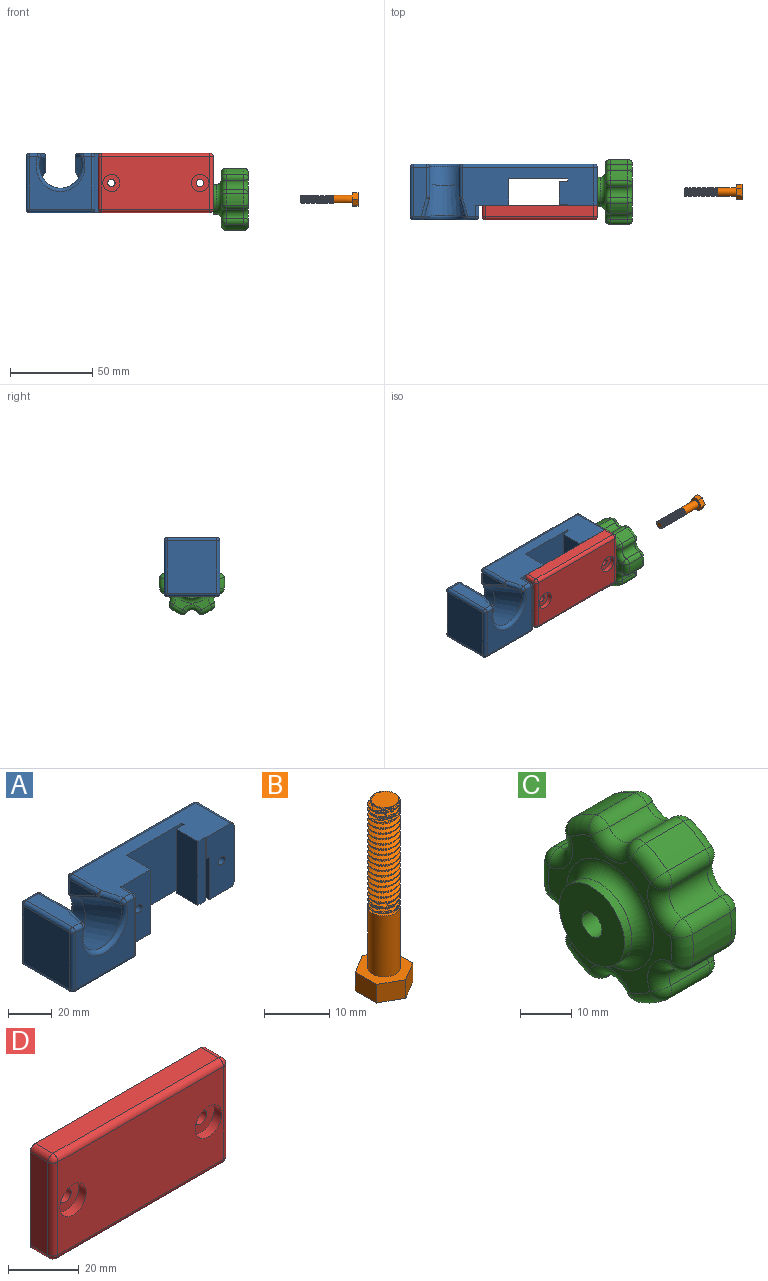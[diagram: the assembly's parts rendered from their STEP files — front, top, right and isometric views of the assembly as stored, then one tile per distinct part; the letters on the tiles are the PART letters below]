
ASSEMBLY  parts=4 mates=3
PART A: 102 faces, bbox 114x44.5x39.6 mm
  f0: cylinder r=2.6mm len=5.5mm, axis (1,0,0), area 89.8mm2, adj f7,f54
  f1: plane 32x23mm, normal (1,0,0), area 640.2mm2, adj f2,f13,f24,f47,f48,f49,f50,f56
  f2: cylinder r=5.5mm len=2.97mm, axis (1,0,0), area 0.3mm2, adj f1,f3,f47
  f3: plane 2.97x0.2mm, normal (1,0,0), area 0.4mm2, adj f2,f47
  f4: cylinder r=2.25mm len=20mm, axis (0,1,0), area 282.7mm2, adj f18,f46
  f5: cylinder r=2.25mm len=20mm, axis (0,1,0), area 282.7mm2, adj f13,f39
  f6: plane 12x1.5mm, normal (-1,0,0), area 18mm2, adj f8,f20,f26,f32
  f7: plane 24x16mm, normal (-1,0,0), area 362.8mm2, adj f0,f8,f13,f21,f26
  f8: plane 38x36mm, normal (0,-1,0), area 1344mm2, adj f6,f7,f19,f20,f21,f26
  f9: cylinder r=2.6mm len=5.4mm, axis (1,0,0), area 88.2mm2, adj f25,f52
  f10: plane 18.62x8.47mm, normal (1,0,0), area 82.6mm2, adj f83,f90,f93,f94
  f11: plane 18.62x8.47mm, normal (-1,0,0), area 82.6mm2, adj f64,f65,f70,f71
  f12: plane 30x8mm, normal (0,0,1), area 220.9mm2, adj f82,f88,f93,f96,f99
  f13: plane 36x18mm, normal (0,-1,0), area 582.4mm2, adj f1,f5,f7,f20,f21,f26,f27,f56
  f14: plane 110x32mm, normal (0,1,0), area 2724.2mm2, adj f33,f34,f35,f36,f37,f38,f40,f41
  f15: plane 32x30mm, normal (-1,0,0), area 960mm2, adj f75,f76,f87,f88
  f16: plane 38x32mm, normal (0,-1,0), area 689.8mm2, adj f73,f74,f86,f87,f95,f96
  f17: plane 32x7mm, normal (1,0,0), area 224mm2, adj f18,f62,f72,f73
  f18: plane 36x20mm, normal (0,-1,0), area 633.8mm2, adj f4,f17,f19,f20,f21,f62,f72
  f19: plane 36x16mm, normal (1,0,0), area 576mm2, adj f8,f18,f20,f21
  f20: plane 80x30mm, normal (0,0,1), area 1370.9mm2, adj f6,f8,f13,f18,f19,f27,f28,f31
  f21: plane 110x30mm, normal (0,0,-1), area 2138mm2, adj f7,f8,f13,f18,f19,f52,f53,f54
  f22: cone r=11.38mm half-angle=3.6deg, axis (0,-0.94,0.34), area 1167.2mm2, adj f23,f70,f85,f94,f95,f99
  f23: cylinder r=11.38mm len=22.76mm, axis (0,0.94,-0.34), area 475.7mm2, adj f22,f65,f70,f77,f90,f94
  f24: cylinder r=5.5mm len=11mm, axis (1,0,0), area 3.1mm2, adj f1,f25,f48
  f25: plane 11x10.7mm, normal (1,0,0), area 73.1mm2, adj f9,f24,f48
  f26: plane 16x2mm, normal (0,0,-1), area 32mm2, adj f6,f7,f8,f13,f27,f30
  f27: plane 12x0.5mm, normal (-1,0,0), area 6mm2, adj f13,f20,f26,f28
  f28: plane 36x5mm, normal (0,-1,0), area 180mm2, adj f20,f27,f29,f30,f31
  f29: plane 14x5mm, normal (0,0,-1), area 60.4mm2, adj f28,f30,f31,f32,f101
  f30: plane 24x14mm, normal (1,0,0), area 336mm2, adj f26,f28,f29,f32
  f31: plane 36x14mm, normal (-1,0,0), area 504mm2, adj f20,f28,f29,f32
  f32: plane 36x5mm, normal (0,1,0), area 180mm2, adj f6,f20,f29,f30,f31
  f33: plane 5x3.9mm, normal (-0.5,0,-0.87), area 22.5mm2, adj f14,f34,f38,f39
  f34: plane 5x4.5mm, normal (-1,0,0), area 22.5mm2, adj f14,f33,f35,f39
  f35: plane 5x3.9mm, normal (-0.5,0,0.87), area 22.5mm2, adj f14,f34,f36,f39
  f36: plane 5x3.9mm, normal (0.5,0,0.87), area 22.5mm2, adj f14,f35,f37,f39
  f37: plane 5x4.5mm, normal (1,0,0), area 22.5mm2, adj f14,f36,f38,f39
  f38: plane 5x3.9mm, normal (0.5,0,-0.87), area 22.5mm2, adj f14,f33,f37,f39
  f39: plane 9.01x7.8mm, normal (0,1,0), area 36.8mm2, adj f5,f33,f34,f35,f36,f37,f38
  f40: plane 5x3.9mm, normal (-0.5,0,-0.87), area 22.5mm2, adj f14,f41,f45,f46
  f41: plane 5x4.5mm, normal (-1,0,0), area 22.5mm2, adj f14,f40,f42,f46
  f42: plane 5x3.9mm, normal (-0.5,0,0.87), area 22.5mm2, adj f14,f41,f43,f46
  f43: plane 5x3.9mm, normal (0.5,0,0.87), area 22.5mm2, adj f14,f42,f44,f46
  f44: plane 5x4.5mm, normal (1,0,0), area 22.5mm2, adj f14,f43,f45,f46
  f45: plane 5x3.9mm, normal (0.5,0,-0.87), area 22.5mm2, adj f14,f40,f44,f46
  f46: plane 9.01x7.8mm, normal (0,1,0), area 36.8mm2, adj f4,f40,f41,f42,f43,f44,f45
  f47: plane 12x11mm, normal (0,0,-1), area 131.7mm2, adj f1,f2,f3,f49,f50,f51
  f48: plane 12x11mm, normal (0,0,1), area 81.6mm2, adj f1,f24,f25,f49,f50,f51,f52,f53
  f49: plane 12x0.1mm, normal (0,1,0), area 1.2mm2, adj f1,f47,f48,f51
  f50: plane 12x0.1mm, normal (0,-1,0), area 1.2mm2, adj f1,f47,f48,f51
  f51: plane 11x0.1mm, normal (1,0,0), area 1.1mm2, adj f47,f48,f49,f50
  f52: plane 13.2x10mm, normal (-1,0,0), area 110.7mm2, adj f9,f21,f48,f53,f55
  f53: plane 13.2x5mm, normal (0,-1,0), area 66mm2, adj f21,f48,f52,f54
  f54: plane 13.2x10mm, normal (1,0,0), area 110.7mm2, adj f0,f21,f48,f53,f55
  f55: plane 13.2x5mm, normal (0,1,0), area 66mm2, adj f21,f48,f52,f54
  f56: cylinder r=2mm len=23mm, axis (0,-1,0), area 72.3mm2, adj f1,f13,f20,f59
  f57: cylinder r=2mm len=23mm, axis (0,1,0), area 72.3mm2, adj f1,f13,f21,f60
  f58: cylinder r=2mm len=32mm, axis (0,0,-1), area 100.5mm2, adj f1,f14,f59,f60
  f59: sphere r=2mm, area 8.6mm2, adj f56,f58,f61
  f60: sphere r=2mm, area 4mm2, adj f57,f58,f63
  f61: cylinder r=2mm len=80mm, axis (1,0,0), area 251.3mm2, adj f14,f20,f59,f66
  f62: cylinder r=2mm len=7mm, axis (0,1,0), area 22mm2, adj f17,f18,f21,f67
  f63: cylinder r=2mm len=110mm, axis (-1,0,0), area 345.6mm2, adj f14,f21,f60,f68
  f64: cylinder r=2mm len=8.47mm, axis (0,0,-1), area 26.6mm2, adj f11,f14,f66,f69
  f65: cylinder r=2mm len=5.08mm, axis (0,0.94,-0.34), area 6mm2, adj f11,f23,f69,f70
  f66: sphere r=2mm, area 6.3mm2, adj f61,f64,f71
  f67: sphere r=2mm, area 6.3mm2, adj f62,f73,f74
  f68: sphere r=2mm, area 4mm2, adj f63,f75,f76
  f69: sphere r=2mm, area 2.5mm2, adj f64,f65,f77
  f70: bspline ~30.39x15.35mm, area 20.4mm2, adj f11,f22,f23,f65,f78
  f71: cylinder r=2mm len=18.62mm, axis (0,-1,0), area 58.5mm2, adj f11,f20,f66,f78
  f72: cylinder r=2mm len=7mm, axis (0,-1,0), area 22mm2, adj f17,f18,f20,f79
  f73: cylinder r=2mm len=32mm, axis (0,0,-1), area 100.5mm2, adj f16,f17,f67,f79
  f74: cylinder r=2mm len=38mm, axis (1,0,0), area 119.4mm2, adj f16,f21,f67,f80
  f75: cylinder r=2mm len=30mm, axis (0,-1,0), area 94.2mm2, adj f15,f21,f68,f80
  f76: cylinder r=2mm len=32mm, axis (0,0,1), area 100.5mm2, adj f14,f15,f68,f81
  f77: bspline ~26.76x22.34mm, area 159.8mm2, adj f14,f23,f69,f84
  f78: sphere r=2mm, area 1.8mm2, adj f70,f71,f85
  f79: sphere r=2mm, area 8.6mm2, adj f72,f73,f86
  f80: sphere r=2mm, area 6.3mm2, adj f74,f75,f87
  f81: sphere r=2mm, area 6.3mm2, adj f76,f82,f88
  f82: cylinder r=2mm len=8mm, axis (1,0,0), area 25.1mm2, adj f12,f14,f81,f89
  f83: cylinder r=2mm len=8.47mm, axis (0,0,-1), area 26.6mm2, adj f10,f14,f84,f89
  f84: sphere r=2mm, area 2.5mm2, adj f77,f83,f90
  f85: bspline ~23.2x9.99mm, area 47mm2, adj f20,f22,f78,f91
  f86: cylinder r=2mm len=4.96mm, axis (-1,0,0), area 15.6mm2, adj f16,f20,f79,f91
  f87: cylinder r=2mm len=32mm, axis (0,0,-1), area 100.5mm2, adj f15,f16,f80,f92
  f88: cylinder r=2mm len=30mm, axis (0,1,0), area 94.2mm2, adj f12,f15,f81,f92
  f89: sphere r=2mm, area 4mm2, adj f82,f83,f93
  f90: cylinder r=2mm len=5.08mm, axis (0,0.94,-0.34), area 6mm2, adj f10,f23,f84,f94
  f91: sphere r=2mm, area 6.9mm2, adj f85,f86,f95
  f92: sphere r=2mm, area 4mm2, adj f87,f88,f96
  f93: cylinder r=2mm len=18.62mm, axis (0,1,0), area 58.5mm2, adj f10,f12,f89,f97
  f94: bspline ~30.39x15.35mm, area 20.4mm2, adj f10,f22,f23,f90,f97
  f95: bspline ~29.79x21.15mm, area 181.1mm2, adj f16,f22,f91,f98
  f96: cylinder r=2mm len=4.96mm, axis (-1,0,0), area 15.6mm2, adj f12,f16,f92,f98
  f97: sphere r=2mm, area 1.8mm2, adj f93,f94,f99
  f98: sphere r=2mm, area 8.3mm2, adj f95,f96,f99
  f99: bspline ~23.2x9.99mm, area 47mm2, adj f12,f22,f97,f98
  f100: plane 3.5x3.5mm, normal (0,0,-1), area 9.6mm2, adj f101
  f101: cylinder r=1.75mm len=31mm, axis (0,0,-1), area 340.9mm2, adj f29,f100
PART B: 34 faces, bbox 8.3x9.5x35.7 mm
  f0: plane 4.03x3.5mm, normal (0.49,0.87,0), area 16.2mm2, adj f1,f5,f6,f7
  f1: plane 3.96x3.5mm, normal (-0.51,0.86,0), area 16.2mm2, adj f0,f2,f6,f7
  f2: plane 4.62x3.5mm, normal (-1,-0.02,0), area 16.2mm2, adj f1,f3,f6,f7
  f3: plane 4.03x3.5mm, normal (-0.49,-0.87,0), area 16.2mm2, adj f2,f4,f6,f7
  f4: plane 3.96x3.5mm, normal (0.51,-0.86,0), area 16.2mm2, adj f3,f5,f6,f7
  f5: plane 4.62x3.5mm, normal (1,0.02,0), area 16.2mm2, adj f0,f4,f6,f7
  f6: plane 9.24x8.07mm, normal (0,0,1), area 35.8mm2, adj f0,f1,f2,f3,f4,f5,f8
  f7: plane 9.24x8.07mm, normal (0,0,-1), area 55.4mm2, adj f0,f1,f2,f3,f4,f5
  f8: cylinder r=2.5mm len=12.5mm, axis (0,0,-1), area 182.5mm2, adj f6,f9,f31,f32,f33
  f9: cylinder r=2.5mm len=5mm, axis (0,0,-1), area 2mm2, adj f8,f10,f31,f32
  f10: cylinder r=2.5mm len=5mm, axis (0,0,-1), area 2mm2, adj f9,f11,f31,f32
  f11: cylinder r=2.5mm len=5mm, axis (0,0,-1), area 2mm2, adj f10,f12,f31,f32
  f12: cylinder r=2.5mm len=5mm, axis (0,0,-1), area 2mm2, adj f11,f13,f31,f32
  f13: cylinder r=2.5mm len=5mm, axis (0,0,-1), area 2mm2, adj f12,f14,f31,f32
  f14: cylinder r=2.5mm len=5mm, axis (0,0,-1), area 2mm2, adj f13,f15,f31,f32
  f15: cylinder r=2.5mm len=5mm, axis (0,0,-1), area 2mm2, adj f14,f16,f31,f32
  f16: cylinder r=2.5mm len=5mm, axis (0,0,-1), area 2mm2, adj f15,f17,f31,f32
  f17: cylinder r=2.5mm len=5mm, axis (0,0,-1), area 2mm2, adj f16,f18,f31,f32
  f18: cylinder r=2.5mm len=5mm, axis (0,0,-1), area 2mm2, adj f17,f19,f31,f32
  f19: cylinder r=2.5mm len=5mm, axis (0,0,-1), area 2mm2, adj f18,f20,f31,f32
  f20: cylinder r=2.5mm len=5mm, axis (0,0,-1), area 2mm2, adj f19,f21,f31,f32
  f21: cylinder r=2.5mm len=5mm, axis (0,0,-1), area 2mm2, adj f20,f22,f31,f32
  f22: cylinder r=2.5mm len=5mm, axis (0,0,-1), area 2mm2, adj f21,f23,f31,f32
  f23: cylinder r=2.5mm len=5mm, axis (0,0,-1), area 2mm2, adj f22,f24,f31,f32
  f24: cylinder r=2.5mm len=5mm, axis (0,0,-1), area 2mm2, adj f23,f25,f31,f32
  f25: cylinder r=2.5mm len=5mm, axis (0,0,-1), area 2mm2, adj f24,f26,f31,f32
  f26: cylinder r=2.5mm len=5mm, axis (0,0,-1), area 2mm2, adj f25,f27,f31,f32
  f27: cylinder r=2.5mm len=5mm, axis (0,0,-1), area 2mm2, adj f26,f28,f31,f32
  f28: cylinder r=2.5mm len=1.75mm, axis (0,0,-1), area 0.1mm2, adj f27,f29,f31
  f29: plane 4.69x4.66mm, normal (0,0,1), area 15.2mm2, adj f28,f30,f31,f32
  f30: bspline ~20.75x4.52mm, area 68mm2, adj f29,f31,f32,f33
  f31: bspline ~20.81x5.77mm, area 175.4mm2, adj f8,f9,f10,f11,f12,f13,f14,f15
  f32: bspline ~20.65x5.77mm, area 174.8mm2, adj f8,f9,f10,f11,f12,f13,f14,f15
  f33: plane 5.27x5.27mm, normal (0,0,1), area 4.5mm2, adj f8,f30,f31,f32
PART C: 91 faces, bbox 21.6x40.6x38.3 mm
  f0: cylinder r=2.75mm len=16.5mm, axis (1,0,0), area 285.1mm2, adj f2,f23
  f1: cylinder r=9mm len=18mm, axis (1,0,0), area 113.1mm2, adj f2,f84
  f2: plane 18x18mm, normal (-1,0,0), area 230.7mm2, adj f0,f1
  f3: plane 34x32mm, normal (1,0,0), area 630mm2, adj f30,f31,f40,f41,f50,f51,f60,f61
  f4: cylinder r=20mm len=10.5mm, axis (1,0,0), area 75.1mm2, adj f69,f78,f79,f83
  f5: cylinder r=4mm len=10.5mm, axis (1,0,0), area 80.9mm2, adj f72,f77,f80,f83
  f6: cylinder r=20mm len=10.5mm, axis (1,0,0), area 75.1mm2, adj f62,f67,f71,f72
  f7: cylinder r=4mm len=10.5mm, axis (1,0,0), area 80.9mm2, adj f52,f57,f61,f62
  f8: cylinder r=20mm len=10.5mm, axis (1,0,0), area 75.1mm2, adj f42,f47,f51,f52
  f9: cylinder r=4mm len=10.5mm, axis (1,0,0), area 80.9mm2, adj f32,f37,f41,f42
  f10: cylinder r=20mm len=10.5mm, axis (1,0,0), area 75.1mm2, adj f24,f27,f31,f32
  f11: cylinder r=4mm len=10.5mm, axis (1,0,0), area 80.9mm2, adj f24,f28,f29,f30
  f12: cylinder r=20mm len=10.5mm, axis (1,0,0), area 75.1mm2, adj f29,f38,f39,f40
  f13: cylinder r=4mm len=10.5mm, axis (1,0,0), area 80.9mm2, adj f39,f48,f49,f50
  f14: cylinder r=20mm len=10.5mm, axis (1,0,0), area 75.1mm2, adj f49,f58,f59,f60
  f15: cylinder r=4mm len=10.5mm, axis (1,0,0), area 80.9mm2, adj f59,f68,f69,f70
  f16: plane 34x32mm, normal (-1,0,0), area 264.2mm2, adj f27,f28,f37,f38,f47,f48,f57,f58
  f17: plane 4.2x4.2mm, normal (0,-0.87,-0.5), area 20.4mm2, adj f18,f22,f23,f87
  f18: plane 4.85x4.2mm, normal (0,0,-1), area 20.4mm2, adj f17,f19,f23,f85
  f19: plane 4.2x4.2mm, normal (0,0.87,-0.5), area 20.4mm2, adj f18,f20,f23,f86
  f20: plane 4.2x4.2mm, normal (0,0.87,0.5), area 20.4mm2, adj f19,f21,f23,f88
  f21: plane 4.85x4.2mm, normal (0,0,1), area 20.4mm2, adj f20,f22,f23,f90
  f22: plane 4.2x4.2mm, normal (0,-0.87,0.5), area 20.4mm2, adj f17,f21,f23,f89
  f23: plane 9.7x8.4mm, normal (1,0,0), area 37.3mm2, adj f0,f17,f18,f19,f20,f21,f22
  f24: cylinder r=3mm len=10.5mm, axis (-1,0,0), area 41.2mm2, adj f10,f11,f25,f26
  f25: sphere r=3mm, area 11.8mm2, adj f24,f27,f28
  f26: sphere r=3mm, area 11.8mm2, adj f24,f30,f31
  f27: torus R=17mm, axis (1,0,0), area 31.9mm2, adj f10,f16,f25,f33
  f28: torus R=7mm, axis (1,0,0), area 46.2mm2, adj f11,f16,f25,f34
  f29: cylinder r=3mm len=10.5mm, axis (-1,0,0), area 41.2mm2, adj f11,f12,f34,f35
  f30: torus R=7mm, axis (1,0,0), area 46.2mm2, adj f3,f11,f26,f35
  f31: torus R=17mm, axis (1,0,0), area 31.9mm2, adj f3,f10,f26,f36
  f32: cylinder r=3mm len=10.5mm, axis (-1,0,0), area 41.2mm2, adj f9,f10,f33,f36
  f33: sphere r=3mm, area 11.8mm2, adj f27,f32,f37
  f34: sphere r=3mm, area 11.8mm2, adj f28,f29,f38
  f35: sphere r=3mm, area 11.8mm2, adj f29,f30,f40
  f36: sphere r=3mm, area 11.8mm2, adj f31,f32,f41
  f37: torus R=7mm, axis (1,0,0), area 46.2mm2, adj f9,f16,f33,f43
  f38: torus R=17mm, axis (1,0,0), area 31.9mm2, adj f12,f16,f34,f44
  f39: cylinder r=3mm len=10.5mm, axis (-1,0,0), area 41.2mm2, adj f12,f13,f44,f45
  f40: torus R=17mm, axis (1,0,0), area 31.9mm2, adj f3,f12,f35,f45
  f41: torus R=7mm, axis (1,0,0), area 46.2mm2, adj f3,f9,f36,f46
  f42: cylinder r=3mm len=10.5mm, axis (-1,0,0), area 41.2mm2, adj f8,f9,f43,f46
  f43: sphere r=3mm, area 11.8mm2, adj f37,f42,f47
  f44: sphere r=3mm, area 11.8mm2, adj f38,f39,f48
  f45: sphere r=3mm, area 11.8mm2, adj f39,f40,f50
  f46: sphere r=3mm, area 11.8mm2, adj f41,f42,f51
  f47: torus R=17mm, axis (1,0,0), area 31.9mm2, adj f8,f16,f43,f53
  f48: torus R=7mm, axis (1,0,0), area 46.2mm2, adj f13,f16,f44,f54
  f49: cylinder r=3mm len=10.5mm, axis (-1,0,0), area 41.2mm2, adj f13,f14,f54,f55
  f50: torus R=7mm, axis (1,0,0), area 46.2mm2, adj f3,f13,f45,f55
  f51: torus R=17mm, axis (1,0,0), area 31.9mm2, adj f3,f8,f46,f56
  f52: cylinder r=3mm len=10.5mm, axis (-1,0,0), area 41.2mm2, adj f7,f8,f53,f56
  f53: sphere r=3mm, area 11.8mm2, adj f47,f52,f57
  f54: sphere r=3mm, area 11.8mm2, adj f48,f49,f58
  f55: sphere r=3mm, area 11.8mm2, adj f49,f50,f60
  f56: sphere r=3mm, area 11.8mm2, adj f51,f52,f61
  f57: torus R=7mm, axis (1,0,0), area 46.2mm2, adj f7,f16,f53,f63
  f58: torus R=17mm, axis (1,0,0), area 31.9mm2, adj f14,f16,f54,f64
  f59: cylinder r=3mm len=10.5mm, axis (-1,0,0), area 41.2mm2, adj f14,f15,f64,f65
  f60: torus R=17mm, axis (1,0,0), area 31.9mm2, adj f3,f14,f55,f65
  f61: torus R=7mm, axis (1,0,0), area 46.2mm2, adj f3,f7,f56,f66
  f62: cylinder r=3mm len=10.5mm, axis (-1,0,0), area 41.2mm2, adj f6,f7,f63,f66
  f63: sphere r=3mm, area 11.8mm2, adj f57,f62,f67
  f64: sphere r=3mm, area 11.8mm2, adj f58,f59,f68
  f65: sphere r=3mm, area 11.8mm2, adj f59,f60,f70
  f66: sphere r=3mm, area 11.8mm2, adj f61,f62,f71
  f67: torus R=17mm, axis (1,0,0), area 31.9mm2, adj f6,f16,f63,f73
  f68: torus R=7mm, axis (1,0,0), area 46.2mm2, adj f15,f16,f64,f74
  f69: cylinder r=3mm len=10.5mm, axis (-1,0,0), area 41.2mm2, adj f4,f15,f74,f75
  f70: torus R=7mm, axis (1,0,0), area 46.2mm2, adj f3,f15,f65,f75
  f71: torus R=17mm, axis (1,0,0), area 31.9mm2, adj f3,f6,f66,f76
  f72: cylinder r=3mm len=10.5mm, axis (-1,0,0), area 41.2mm2, adj f5,f6,f73,f76
  f73: sphere r=3mm, area 11.8mm2, adj f67,f72,f77
  f74: sphere r=3mm, area 11.8mm2, adj f68,f69,f78
  f75: sphere r=3mm, area 11.8mm2, adj f69,f70,f79
  f76: sphere r=3mm, area 11.8mm2, adj f71,f72,f80
  f77: torus R=7mm, axis (1,0,0), area 46.2mm2, adj f5,f16,f73,f81
  f78: torus R=17mm, axis (1,0,0), area 31.9mm2, adj f4,f16,f74,f81
  f79: torus R=17mm, axis (1,0,0), area 31.9mm2, adj f3,f4,f75,f82
  f80: torus R=7mm, axis (1,0,0), area 46.2mm2, adj f3,f5,f76,f82
  f81: sphere r=3mm, area 11.8mm2, adj f77,f78,f83
  f82: sphere r=3mm, area 11.8mm2, adj f79,f80,f83
  f83: cylinder r=3mm len=10.5mm, axis (-1,0,0), area 41.2mm2, adj f4,f5,f81,f82
  f84: torus R=12mm, axis (1,0,0), area 298.8mm2, adj f1,f16
  f85: cylinder r=0.8mm len=5.77mm, axis (0,1,0), area 6.5mm2, adj f3,f18,f86,f87
  f86: cylinder r=0.8mm len=5.4mm, axis (0,0.5,0.87), area 6.5mm2, adj f3,f19,f85,f88
  f87: cylinder r=0.8mm len=5.4mm, axis (0,0.5,-0.87), area 6.5mm2, adj f3,f17,f85,f89
  f88: cylinder r=0.8mm len=5.4mm, axis (0,-0.5,0.87), area 6.5mm2, adj f3,f20,f86,f90
  f89: cylinder r=0.8mm len=5.4mm, axis (0,-0.5,-0.87), area 6.5mm2, adj f3,f22,f87,f90
  f90: cylinder r=0.8mm len=5.77mm, axis (0,-1,0), area 6.5mm2, adj f3,f21,f88,f89
PART D: 24 faces, bbox 70x9x36 mm
  f0: cylinder r=2.25mm len=6mm, axis (0,1,0), area 84.8mm2, adj f6,f11
  f1: cylinder r=2.25mm len=6mm, axis (0,1,0), area 84.8mm2, adj f6,f9
  f2: plane 66x7mm, normal (0,0,1), area 462mm2, adj f6,f18,f19,f23
  f3: plane 32x7mm, normal (-1,0,0), area 224mm2, adj f6,f12,f17,f18
  f4: plane 66x7mm, normal (0,0,-1), area 462mm2, adj f6,f12,f13,f14
  f5: plane 66x32mm, normal (0,-1,0), area 1938.8mm2, adj f8,f10,f14,f17,f20,f23
  f6: plane 70x36mm, normal (0,1,0), area 2484.8mm2, adj f0,f1,f2,f3,f4,f7,f12,f13
  f7: plane 32x7mm, normal (1,0,0), area 224mm2, adj f6,f13,f19,f20
  f8: cylinder r=5.25mm len=10.5mm, axis (0,-1,0), area 99mm2, adj f5,f9
  f9: plane 10.5x10.5mm, normal (0,-1,0), area 70.7mm2, adj f1,f8
  f10: cylinder r=5.25mm len=10.5mm, axis (0,-1,0), area 99mm2, adj f5,f11
  f11: plane 10.5x10.5mm, normal (0,-1,0), area 70.7mm2, adj f0,f10
  f12: cylinder r=2mm len=7mm, axis (0,-1,0), area 22mm2, adj f3,f4,f6,f15
  f13: cylinder r=2mm len=7mm, axis (0,1,0), area 22mm2, adj f4,f6,f7,f16
  f14: cylinder r=2mm len=66mm, axis (1,0,0), area 207.3mm2, adj f4,f5,f15,f16
  f15: sphere r=2mm, area 6.3mm2, adj f12,f14,f17
  f16: sphere r=2mm, area 6.3mm2, adj f13,f14,f20
  f17: cylinder r=2mm len=32mm, axis (0,0,-1), area 100.5mm2, adj f3,f5,f15,f21
  f18: cylinder r=2mm len=7mm, axis (0,1,0), area 22mm2, adj f2,f3,f6,f21
  f19: cylinder r=2mm len=7mm, axis (0,-1,0), area 22mm2, adj f2,f6,f7,f22
  f20: cylinder r=2mm len=32mm, axis (0,0,1), area 100.5mm2, adj f5,f7,f16,f22
  f21: sphere r=2mm, area 6.3mm2, adj f17,f18,f23
  f22: sphere r=2mm, area 6.3mm2, adj f19,f20,f23
  f23: cylinder r=2mm len=66mm, axis (-1,0,0), area 207.3mm2, adj f2,f5,f21,f22
PLACE A t=(-23.53,-32.33,17.16)mm
PLACE B rot(axis=(0,-1,0),90deg) t=(58.18,-24.83,12.12)mm
PLACE C rot(axis=(1,0,0),180deg) t=(-8.53,-24.83,25.16)mm
PLACE D t=(-23.53,-32.33,17.16)mm
MATE fastened C.f1 <-> A.f0  axis (-1,0,0) through (-30.03,-24.83,25.16)mm
MATE cylindrical D.f1 <-> A.f4  axis (0,1,0) through (-92.03,-32.83,35.16)mm
MATE cylindrical B.f8 <-> C.f1  axis (-1,0,0) through (23.18,-24.83,25.16)mm
